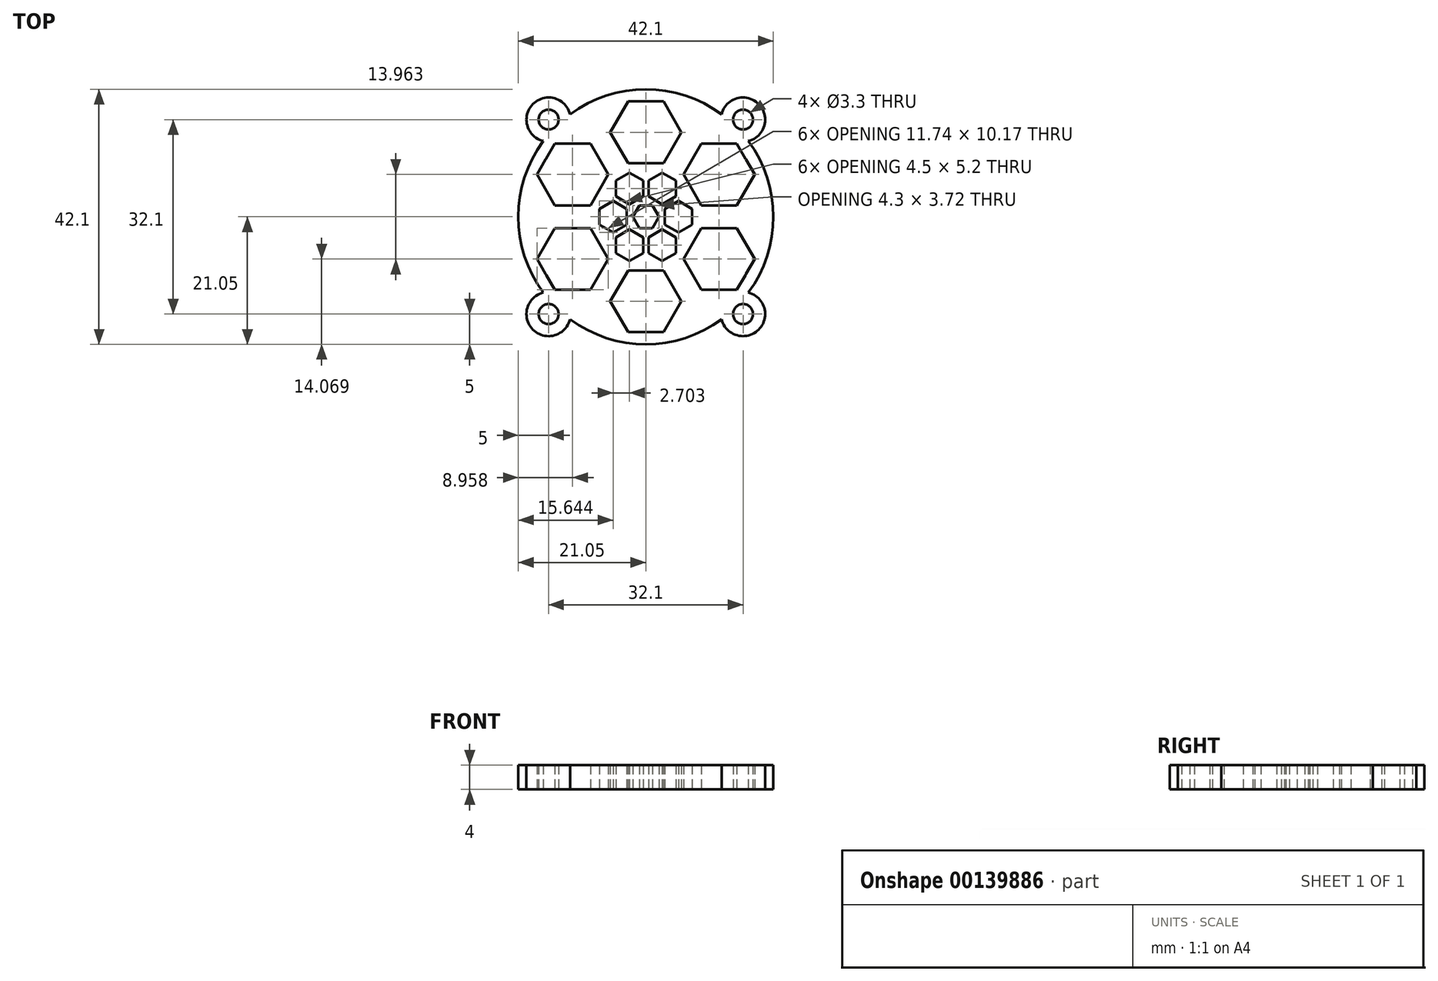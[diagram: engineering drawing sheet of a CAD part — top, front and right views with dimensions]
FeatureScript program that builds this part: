
annotation { "Feature Type Name" : "Feature", "Feature Type Description" : "" }
export const myFeature = defineFeature(function(context is Context, id is Id, definition is map)
    precondition{}
    {
        {
            var Q0;
            Q0=qCreatedBy(makeId("Top.planeOp"),FACE);
            var sketch = newSketch(context, id + "F0", { "sketchPlane" : qUnion([Q0])});
            skCircle(sketch, "E0", {"center": v(-16.05, -16.05) * mm, "radius": 1.65 * mm});
            skCircle(sketch, "E1", {"center": v(0, 0) * mm, "radius": 21.05 * mm});
            skCircle(sketch, "E2", {"center": v(0, 0) * mm, "radius": 19.05 * mm});
            skCircle(sketch, "E3.cCircle", {"center": v(0, 13.96) * mm, "radius": 5.09 * mm, "construction": true});
            skLineSegment(sketch, "E3.0", {"start": v(-2.94, 19.05) * mm, "end": v(2.94, 19.05) * mm});
            skLineSegment(sketch, "E3.1", {"start": v(2.94, 19.05) * mm, "end": v(5.87, 13.96) * mm});
            skLineSegment(sketch, "E3.2", {"start": v(5.87, 13.96) * mm, "end": v(2.94, 8.88) * mm});
            skLineSegment(sketch, "E3.3", {"start": v(2.94, 8.88) * mm, "end": v(-2.94, 8.88) * mm});
            skLineSegment(sketch, "E3.4", {"start": v(-2.94, 8.88) * mm, "end": v(-5.87, 13.96) * mm});
            skLineSegment(sketch, "E3.5", {"start": v(-5.87, 13.96) * mm, "end": v(-2.94, 19.05) * mm});
            skPoint(sketch, "E3.0.midPoint", {"position": v(0, 19.05) * mm});
            skLineSegment(sketch, "E4.1.0", {"start": v(9.16, 12.07) * mm, "end": v(15.03, 12.07) * mm});
            skLineSegment(sketch, "E4.1.1", {"start": v(15.03, 1.9) * mm, "end": v(9.16, 1.9) * mm});
            skLineSegment(sketch, "E4.1.2", {"start": v(9.16, 1.9) * mm, "end": v(6.22, 6.98) * mm});
            skLineSegment(sketch, "E4.1.3", {"start": v(15.03, 12.07) * mm, "end": v(17.96, 6.98) * mm});
            skLineSegment(sketch, "E4.1.4", {"start": v(6.22, 6.98) * mm, "end": v(9.16, 12.07) * mm});
            skLineSegment(sketch, "E4.1.5", {"start": v(17.96, 6.98) * mm, "end": v(15.03, 1.9) * mm});
            skLineSegment(sketch, "E4.2.0", {"start": v(15.03, -1.9) * mm, "end": v(17.96, -6.98) * mm});
            skLineSegment(sketch, "E4.2.1", {"start": v(9.16, -12.07) * mm, "end": v(6.22, -6.98) * mm});
            skLineSegment(sketch, "E4.2.2", {"start": v(6.22, -6.98) * mm, "end": v(9.16, -1.9) * mm});
            skLineSegment(sketch, "E4.2.3", {"start": v(17.96, -6.98) * mm, "end": v(15.03, -12.07) * mm});
            skLineSegment(sketch, "E4.2.4", {"start": v(9.16, -1.9) * mm, "end": v(15.03, -1.9) * mm});
            skLineSegment(sketch, "E4.2.5", {"start": v(15.03, -12.07) * mm, "end": v(9.16, -12.07) * mm});
            skLineSegment(sketch, "E4.3.0", {"start": v(5.87, -13.96) * mm, "end": v(2.94, -19.05) * mm});
            skLineSegment(sketch, "E4.3.1", {"start": v(-5.87, -13.96) * mm, "end": v(-2.94, -8.88) * mm});
            skLineSegment(sketch, "E4.3.2", {"start": v(-2.94, -8.88) * mm, "end": v(2.94, -8.88) * mm});
            skLineSegment(sketch, "E4.3.3", {"start": v(2.94, -19.05) * mm, "end": v(-2.94, -19.05) * mm});
            skLineSegment(sketch, "E4.3.4", {"start": v(2.94, -8.88) * mm, "end": v(5.87, -13.96) * mm});
            skLineSegment(sketch, "E4.3.5", {"start": v(-2.94, -19.05) * mm, "end": v(-5.87, -13.96) * mm});
            skLineSegment(sketch, "E4.4.0", {"start": v(-9.16, -12.07) * mm, "end": v(-15.03, -12.07) * mm});
            skLineSegment(sketch, "E4.4.1", {"start": v(-15.03, -1.9) * mm, "end": v(-9.16, -1.9) * mm});
            skLineSegment(sketch, "E4.4.2", {"start": v(-9.16, -1.9) * mm, "end": v(-6.22, -6.98) * mm});
            skLineSegment(sketch, "E4.4.3", {"start": v(-15.03, -12.07) * mm, "end": v(-17.96, -6.98) * mm});
            skLineSegment(sketch, "E4.4.4", {"start": v(-6.22, -6.98) * mm, "end": v(-9.16, -12.07) * mm});
            skLineSegment(sketch, "E4.4.5", {"start": v(-17.96, -6.98) * mm, "end": v(-15.03, -1.9) * mm});
            skLineSegment(sketch, "E4.5.0", {"start": v(-15.03, 1.9) * mm, "end": v(-17.96, 6.98) * mm});
            skLineSegment(sketch, "E4.5.1", {"start": v(-9.16, 12.07) * mm, "end": v(-6.22, 6.98) * mm});
            skLineSegment(sketch, "E4.5.2", {"start": v(-6.22, 6.98) * mm, "end": v(-9.16, 1.9) * mm});
            skLineSegment(sketch, "E4.5.3", {"start": v(-17.96, 6.98) * mm, "end": v(-15.03, 12.07) * mm});
            skLineSegment(sketch, "E4.5.4", {"start": v(-9.16, 1.9) * mm, "end": v(-15.03, 1.9) * mm});
            skLineSegment(sketch, "E4.5.5", {"start": v(-15.03, 12.07) * mm, "end": v(-9.16, 12.07) * mm});
            skLineSegment(sketch, "E4.anchor1", {"start": v(0, 0) * mm, "end": v(-2.94, 19.05) * mm, "construction": true});
            skLineSegment(sketch, "E4.anchor2", {"start": v(0, 0) * mm, "end": v(-17.96, 6.98) * mm, "construction": true});
            skLineSegment(sketch, "E5", {"start": v(2.94, 8.88) * mm, "end": v(6.22, 6.98) * mm, "construction": true});
            skLineSegment(sketch, "E6", {"start": v(-16.05, -16.05) * mm, "end": v(0, 0) * mm, "construction": true});
            skCircle(sketch, "E7", {"center": v(-16.05, -16.05) * mm, "radius": 3.65 * mm});
            skCircle(sketch, "E8.0.1.0", {"center": v(-16.05, 16.05) * mm, "radius": 3.65 * mm});
            skCircle(sketch, "E8.0.1.1", {"center": v(-16.05, 16.05) * mm, "radius": 1.65 * mm});
            skCircle(sketch, "E8.1.0.0", {"center": v(16.05, -16.05) * mm, "radius": 3.65 * mm});
            skCircle(sketch, "E8.1.0.1", {"center": v(16.05, -16.05) * mm, "radius": 1.65 * mm});
            skCircle(sketch, "E8.1.1.0", {"center": v(16.05, 16.05) * mm, "radius": 3.65 * mm});
            skCircle(sketch, "E8.1.1.1", {"center": v(16.05, 16.05) * mm, "radius": 1.65 * mm});
            skLineSegment(sketch, "E8.direction1", {"start": v(-16.05, -16.05) * mm, "end": v(16.05, -16.05) * mm, "construction": true});
            skLineSegment(sketch, "E8.direction2", {"start": v(-16.05, -16.05) * mm, "end": v(-16.05, 16.05) * mm, "construction": true});
            skCircle(sketch, "E9.cCircle", {"center": v(2.7, 4.68) * mm, "radius": 2.25 * mm, "construction": true});
            skLineSegment(sketch, "E9.0", {"start": v(2.7, 7.28) * mm, "end": v(4.95, 5.98) * mm});
            skLineSegment(sketch, "E9.1", {"start": v(4.95, 5.98) * mm, "end": v(4.95, 3.38) * mm});
            skLineSegment(sketch, "E9.2", {"start": v(4.95, 3.38) * mm, "end": v(2.7, 2.08) * mm});
            skLineSegment(sketch, "E9.3", {"start": v(2.7, 2.08) * mm, "end": v(0.45, 3.38) * mm});
            skLineSegment(sketch, "E9.4", {"start": v(0.45, 3.38) * mm, "end": v(0.45, 5.98) * mm});
            skLineSegment(sketch, "E9.5", {"start": v(0.45, 5.98) * mm, "end": v(2.7, 7.28) * mm});
            skPoint(sketch, "E9.0.midPoint", {"position": v(3.83, 6.63) * mm});
            skLineSegment(sketch, "E10", {"start": v(3.83, 6.63) * mm, "end": v(4.58, 7.93) * mm, "construction": true});
            skCircle(sketch, "E11.cCircle", {"center": v(0, 0) * mm, "radius": 1.86 * mm, "construction": true});
            skLineSegment(sketch, "E11.0", {"start": v(-1.08, 1.86) * mm, "end": v(1.08, 1.86) * mm});
            skLineSegment(sketch, "E11.1", {"start": v(1.08, 1.86) * mm, "end": v(2.15, 0) * mm});
            skLineSegment(sketch, "E11.2", {"start": v(2.15, 0) * mm, "end": v(1.08, -1.86) * mm});
            skLineSegment(sketch, "E11.3", {"start": v(1.08, -1.86) * mm, "end": v(-1.08, -1.86) * mm});
            skLineSegment(sketch, "E11.4", {"start": v(-1.08, -1.86) * mm, "end": v(-2.15, 0) * mm});
            skLineSegment(sketch, "E11.5", {"start": v(-2.15, 0) * mm, "end": v(-1.08, 1.86) * mm});
            skPoint(sketch, "E11.0.midPoint", {"position": v(0, 1.86) * mm});
            skLineSegment(sketch, "E12", {"start": v(1.08, 1.86) * mm, "end": v(1.58, 2.73) * mm, "construction": true});
            skLineSegment(sketch, "E13.1.0", {"start": v(-4.95, 3.38) * mm, "end": v(-4.95, 5.98) * mm});
            skLineSegment(sketch, "E13.1.1", {"start": v(-4.95, 5.98) * mm, "end": v(-2.7, 7.28) * mm});
            skLineSegment(sketch, "E13.1.2", {"start": v(-2.7, 7.28) * mm, "end": v(-0.45, 5.98) * mm});
            skLineSegment(sketch, "E13.1.3", {"start": v(-0.45, 5.98) * mm, "end": v(-0.45, 3.38) * mm});
            skLineSegment(sketch, "E13.1.4", {"start": v(-0.45, 3.38) * mm, "end": v(-2.7, 2.08) * mm});
            skLineSegment(sketch, "E13.1.5", {"start": v(-2.7, 2.08) * mm, "end": v(-4.95, 3.38) * mm});
            skLineSegment(sketch, "E13.2.0", {"start": v(-5.4, -2.6) * mm, "end": v(-7.66, -1.3) * mm});
            skLineSegment(sketch, "E13.2.1", {"start": v(-7.66, -1.3) * mm, "end": v(-7.66, 1.3) * mm});
            skLineSegment(sketch, "E13.2.2", {"start": v(-7.66, 1.3) * mm, "end": v(-5.4, 2.6) * mm});
            skLineSegment(sketch, "E13.2.3", {"start": v(-5.4, 2.6) * mm, "end": v(-3.16, 1.3) * mm});
            skLineSegment(sketch, "E13.2.4", {"start": v(-3.16, 1.3) * mm, "end": v(-3.16, -1.3) * mm});
            skLineSegment(sketch, "E13.2.5", {"start": v(-3.16, -1.3) * mm, "end": v(-5.4, -2.6) * mm});
            skLineSegment(sketch, "E13.3.0", {"start": v(-0.45, -5.98) * mm, "end": v(-2.7, -7.28) * mm});
            skLineSegment(sketch, "E13.3.1", {"start": v(-2.7, -7.28) * mm, "end": v(-4.95, -5.98) * mm});
            skLineSegment(sketch, "E13.3.2", {"start": v(-4.95, -5.98) * mm, "end": v(-4.95, -3.38) * mm});
            skLineSegment(sketch, "E13.3.3", {"start": v(-4.95, -3.38) * mm, "end": v(-2.7, -2.08) * mm});
            skLineSegment(sketch, "E13.3.4", {"start": v(-2.7, -2.08) * mm, "end": v(-0.45, -3.38) * mm});
            skLineSegment(sketch, "E13.3.5", {"start": v(-0.45, -3.38) * mm, "end": v(-0.45, -5.98) * mm});
            skLineSegment(sketch, "E13.4.0", {"start": v(4.95, -3.38) * mm, "end": v(4.95, -5.98) * mm});
            skLineSegment(sketch, "E13.4.1", {"start": v(4.95, -5.98) * mm, "end": v(2.7, -7.28) * mm});
            skLineSegment(sketch, "E13.4.2", {"start": v(2.7, -7.28) * mm, "end": v(0.45, -5.98) * mm});
            skLineSegment(sketch, "E13.4.3", {"start": v(0.45, -5.98) * mm, "end": v(0.45, -3.38) * mm});
            skLineSegment(sketch, "E13.4.4", {"start": v(0.45, -3.38) * mm, "end": v(2.7, -2.08) * mm});
            skLineSegment(sketch, "E13.4.5", {"start": v(2.7, -2.08) * mm, "end": v(4.95, -3.38) * mm});
            skLineSegment(sketch, "E13.5.0", {"start": v(5.4, 2.6) * mm, "end": v(7.66, 1.3) * mm});
            skLineSegment(sketch, "E13.5.1", {"start": v(7.66, 1.3) * mm, "end": v(7.66, -1.3) * mm});
            skLineSegment(sketch, "E13.5.2", {"start": v(7.66, -1.3) * mm, "end": v(5.4, -2.6) * mm});
            skLineSegment(sketch, "E13.5.3", {"start": v(5.4, -2.6) * mm, "end": v(3.16, -1.3) * mm});
            skLineSegment(sketch, "E13.5.4", {"start": v(3.16, -1.3) * mm, "end": v(3.16, 1.3) * mm});
            skLineSegment(sketch, "E13.5.5", {"start": v(3.16, 1.3) * mm, "end": v(5.4, 2.6) * mm});
            skSolve(sketch);
        }
        {
            var Q0;
            {var subQ0=sQuery(id+"F0.wireOp",EDGE,"E8.0.1.0");var subQ1=sQuery(id+"F0.wireOp",EDGE,"E1");var subQ2=makeQuery(id+"F0.imprint","INTERSECT",VERTEX,{"disambiguationData":[OD(0.0)],"derivedFrom":[subQ1,subQ0]});Q0=makeQuery(id+"F0.imprint","IMPRINT",FACE,{"disambiguationData":[TD([[makeQuery(id+"F0.imprint","IMPRINT",EDGE,{"disambiguationData":[TD([[subQ2,-1.0]])],"derivedFrom":subQ1}),1.0]])]});}
            var Q1;
            {var subQ8=sQuery(id+"F0.wireOp",EDGE,"E8.1.1.0");var subQ12=sQuery(id+"F0.wireOp",EDGE,"E1");var subQ13=makeQuery(id+"F0.imprint","INTERSECT",VERTEX,{"disambiguationData":[OD(1.0)],"derivedFrom":[subQ12,subQ8]});Q1=makeQuery(id+"F0.imprint","IMPRINT",FACE,{"disambiguationData":[TD([[makeQuery(id+"F0.imprint","IMPRINT",EDGE,{"disambiguationData":[TD([[subQ13,-1.0]])],"derivedFrom":subQ12}),1.0]])]});}
            var Q2;
            {var subQ0=sQuery(id+"F0.wireOp",EDGE,"E1");var subQ1=makeQuery(id+"F0.imprint","INTERSECT",VERTEX,{"derivedFrom":[subQ0,sQuery(id+"F0.wireOp",EDGE,"E8.1.1.1")]});Q2=makeQuery(id+"F0.imprint","IMPRINT",FACE,{"disambiguationData":[TD([[makeQuery(id+"F0.imprint","IMPRINT",EDGE,{"disambiguationData":[TD([[subQ1,1.0]])],"derivedFrom":subQ0}),1.0]])]});}
            var Q3;
            {var subQ8=sQuery(id+"F0.wireOp",EDGE,"E8.1.1.0");var subQ9=sQuery(id+"F0.wireOp",EDGE,"E1");var subQ10=makeQuery(id+"F0.imprint","INTERSECT",VERTEX,{"disambiguationData":[OD(0.0)],"derivedFrom":[subQ9,subQ8]});Q3=makeQuery(id+"F0.imprint","IMPRINT",FACE,{"disambiguationData":[TD([[makeQuery(id+"F0.imprint","IMPRINT",EDGE,{"disambiguationData":[TD([[subQ10,1.0]])],"derivedFrom":subQ9}),1.0]])]});}
            var Q4;
            {var subQ0=sQuery(id+"F0.wireOp",EDGE,"E8.1.0.0");var subQ1=sQuery(id+"F0.wireOp",EDGE,"E1");var subQ2=makeQuery(id+"F0.imprint","INTERSECT",VERTEX,{"disambiguationData":[OD(0.0)],"derivedFrom":[subQ1,subQ0]});Q4=makeQuery(id+"F0.imprint","IMPRINT",FACE,{"disambiguationData":[TD([[makeQuery(id+"F0.imprint","IMPRINT",EDGE,{"disambiguationData":[TD([[subQ2,-1.0]])],"derivedFrom":subQ1}),1.0]])]});}
            var Q5;
            {var subQ11=sQuery(id+"F0.wireOp",EDGE,"E7");var subQ13=sQuery(id+"F0.wireOp",EDGE,"E1");var subQ14=makeQuery(id+"F0.imprint","INTERSECT",VERTEX,{"disambiguationData":[OD(1.0)],"derivedFrom":[subQ13,subQ11]});Q5=makeQuery(id+"F0.imprint","IMPRINT",FACE,{"disambiguationData":[TD([[makeQuery(id+"F0.imprint","IMPRINT",EDGE,{"disambiguationData":[TD([[subQ14,-1.0]])],"derivedFrom":subQ13}),1.0]])]});}
            var Q6;
            {var subQ0=sQuery(id+"F0.wireOp",EDGE,"E1");var subQ1=makeQuery(id+"F0.imprint","INTERSECT",VERTEX,{"derivedFrom":[sQuery(id+"F0.wireOp",EDGE,"E0"),subQ0]});Q6=makeQuery(id+"F0.imprint","IMPRINT",FACE,{"disambiguationData":[TD([[makeQuery(id+"F0.imprint","IMPRINT",EDGE,{"disambiguationData":[TD([[subQ1,1.0]])],"derivedFrom":subQ0}),1.0]])]});}
            var Q7;
            {var subQ8=sQuery(id+"F0.wireOp",EDGE,"E8.0.1.0");var subQ14=sQuery(id+"F0.wireOp",EDGE,"E1");var subQ15=makeQuery(id+"F0.imprint","INTERSECT",VERTEX,{"disambiguationData":[OD(1.0)],"derivedFrom":[subQ14,subQ8]});Q7=makeQuery(id+"F0.imprint","IMPRINT",FACE,{"disambiguationData":[TD([[makeQuery(id+"F0.imprint","IMPRINT",EDGE,{"disambiguationData":[TD([[subQ15,-1.0]])],"derivedFrom":subQ14}),1.0]])]});}
            var Q8;
            {var subQ3=sQuery(id+"F0.wireOp",EDGE,"E8.0.1.1");Q8=makeQuery(id+"F0.imprint","IMPRINT",FACE,{"disambiguationData":[TD([[makeQuery(id+"F0.imprint","IMPRINT",EDGE,{"derivedFrom":subQ3}),-1.0]])]});}
            var Q9;
            {var subQ0=sQuery(id+"F0.wireOp",EDGE,"E8.1.1.1");Q9=makeQuery(id+"F0.imprint","IMPRINT",FACE,{"disambiguationData":[TD([[makeQuery(id+"F0.imprint","IMPRINT",EDGE,{"derivedFrom":subQ0}),-1.0]])]});}
            var Q10;
            {var subQ3=sQuery(id+"F0.wireOp",EDGE,"E8.1.0.1");Q10=makeQuery(id+"F0.imprint","IMPRINT",FACE,{"disambiguationData":[TD([[makeQuery(id+"F0.imprint","IMPRINT",EDGE,{"derivedFrom":subQ3}),-1.0]])]});}
            var Q11;
            {var subQ0=sQuery(id+"F0.wireOp",EDGE,"E0");Q11=makeQuery(id+"F0.imprint","IMPRINT",FACE,{"disambiguationData":[TD([[makeQuery(id+"F0.imprint","IMPRINT",EDGE,{"derivedFrom":subQ0}),-1.0]])]});}
            var Q12;
            {var subQ39=sQuery(id+"F0.wireOp",EDGE,"E3.2");Q12=makeQuery(id+"F0.imprint","IMPRINT",FACE,{"disambiguationData":[TD([[makeQuery(id+"F0.imprint","IMPRINT",EDGE,{"derivedFrom":subQ39}),1.0]])]});}
            extrude(context, id + "F1", {"entities" : qUnion([Q0, Q1, Q2, Q3, Q4, Q5, Q6, Q7, Q8, Q9, Q10, Q11, Q12]), "depth" : 4 * mm});
        }
    });
